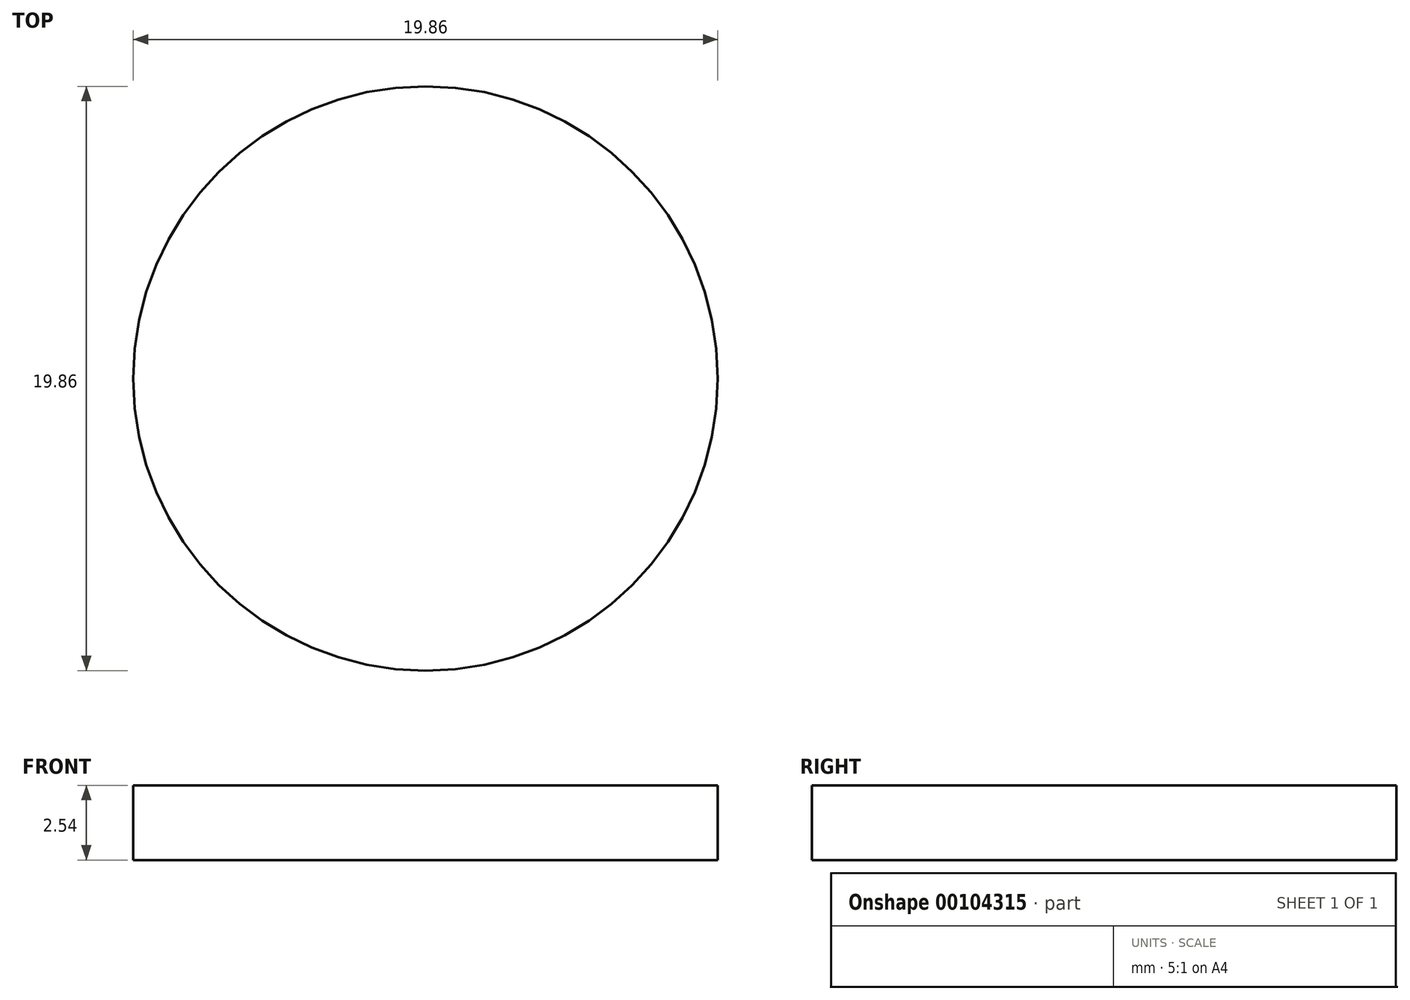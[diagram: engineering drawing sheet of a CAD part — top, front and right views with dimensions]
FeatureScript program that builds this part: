
annotation { "Feature Type Name" : "Feature", "Feature Type Description" : "" }
export const myFeature = defineFeature(function(context is Context, id is Id, definition is map)
    precondition{}
    {
        {
            var Q0;
            Q0=qCreatedBy(makeId("Top.planeOp"),FACE);
            var sketch = newSketch(context, id + "F0", { "sketchPlane" : qUnion([Q0])});
            skCircle(sketch, "E0", {"center": v(0, 0) * mm, "radius": 9.93 * mm});
            skSolve(sketch);
        }
        {
            var Q0;
            Q0=makeQuery(id+"F0.imprint","IMPRINT",FACE,{"disambiguationData":[TD([[makeQuery(id+"F0.imprint","IMPRINT",EDGE,{"derivedFrom":sQuery(id+"F0.wireOp",EDGE,"E0")}),1.0]])]});
            extrude(context, id + "F1", {"entities" : qUnion([Q0]), "depth" : 2.54 * mm});
        }
    });
